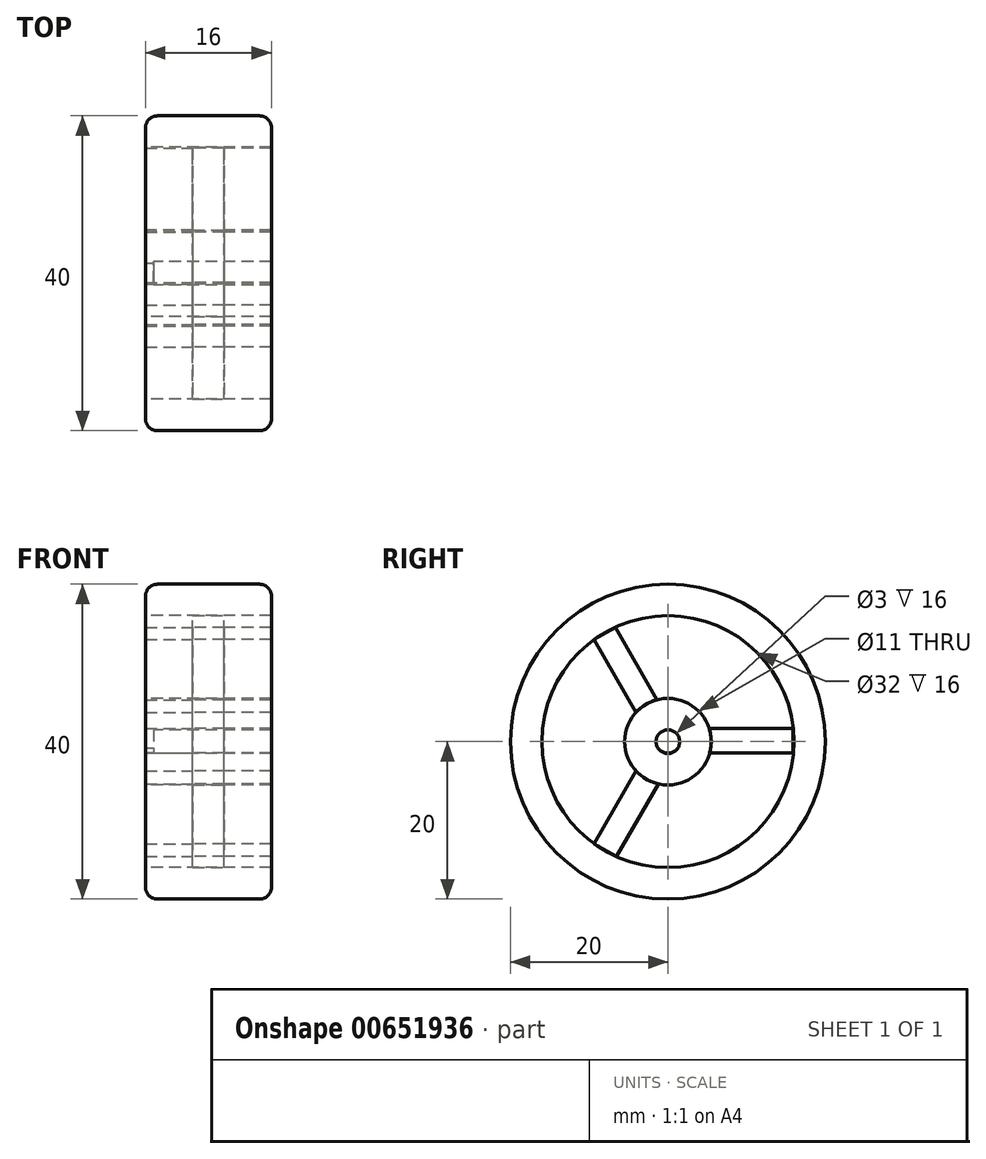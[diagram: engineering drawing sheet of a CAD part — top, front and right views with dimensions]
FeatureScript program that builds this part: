
annotation { "Feature Type Name" : "Feature", "Feature Type Description" : "" }
export const myFeature = defineFeature(function(context is Context, id is Id, definition is map)
    precondition{}
    {
        {
            var Q0;
            Q0=qCreatedBy(makeId("Front.planeOp"),FACE);
            var sketch = newSketch(context, id + "F0", { "sketchPlane" : qUnion([Q0])});
            skLineSegment(sketch, "E0.bottom", {"start": v(0, 0) * mm, "end": v(16, 0) * mm});
            skLineSegment(sketch, "E1.bottom", {"start": v(6, 0) * mm, "end": v(10, 0) * mm});
            skLineSegment(sketch, "E1.top", {"start": v(6, -16) * mm, "end": v(10, -16) * mm});
            skLineSegment(sketch, "E1.left", {"start": v(6, -13) * mm, "end": v(6, -14.5) * mm});
            skLineSegment(sketch, "E1.right", {"start": v(10, -13) * mm, "end": v(10, -14.5) * mm});
            skLineSegment(sketch, "E2.bottom", {"start": v(0, -16) * mm, "end": v(16, -16) * mm, "construction": true});
            skLineSegment(sketch, "E2.top", {"start": v(0, -13) * mm, "end": v(16, -13) * mm});
            skLineSegment(sketch, "E2.left", {"start": v(0, -14.5) * mm, "end": v(0, -13) * mm});
            skLineSegment(sketch, "E3", {"start": v(16, -14.5) * mm, "end": v(0, -14.5) * mm});
            skLineSegment(sketch, "E4", {"start": v(16, -14.5) * mm, "end": v(16, -13) * mm});
            skLineSegment(sketch, "E5.bottom", {"start": v(10, -13) * mm, "end": v(6, -13) * mm});
            skLineSegment(sketch, "E5.top", {"start": v(10, -10.5) * mm, "end": v(6, -10.5) * mm});
            skLineSegment(sketch, "E5.left", {"start": v(10, -13) * mm, "end": v(10, -10.5) * mm});
            skLineSegment(sketch, "E5.right", {"start": v(6, -13) * mm, "end": v(6, -10.5) * mm});
            skArc(sketch, "E6", {"start": v(1.5, 4) * mm, "mid": v(0.44, 3.56) * mm, "end": v(0, 2.5) * mm});
            skLineSegment(sketch, "E7", {"start": v(16, 4.74) * mm, "end": v(14.5, 4.74) * mm});
            skArc(sketch, "E8", {"start": v(16, 2.5) * mm, "mid": v(15.56, 3.56) * mm, "end": v(14.5, 4) * mm});
            skLineSegment(sketch, "E9", {"start": v(0, 2.5) * mm, "end": v(0, 0) * mm});
            skLineSegment(sketch, "E10", {"start": v(16, 0) * mm, "end": v(16, 2.5) * mm});
            skLineSegment(sketch, "E11", {"start": v(14.5, 4) * mm, "end": v(1.5, 4) * mm});
            skPoint(sketch, "E12.end.orphan", {"position": v(8, 0) * mm});
            skPoint(sketch, "E12.start.orphan", {"position": v(8, -10.5) * mm});
            skSolve(sketch);
        }
        {
            var Q0;
            Q0=qSketchRegion(id+"F0",true);
            var Q1;
            Q1=sQuery(id+"F0.wireOp",EDGE,"E1.top");
            revolve(context, id + "F1", {"entities" : qUnion([Q0]), "axis" : qUnion([Q1]), "revolveType" : RevolveType.FULL});
        }
        {
            var Q0;
            Q0=makeQuery(id+"F1.opRevolve","SWEPT_FACE",FACE,{"disambiguationData":[OSD([sQuery(id+"F0.wireOp",EDGE,"E5.right"),sQuery(id+"F0.wireOp",EDGE,"ZnnQBpbw-xC8R-MT8B-JQXv-VcrKk8POS6gG")])]});
            var sketch = newSketch(context, id + "F2", { "sketchPlane" : qUnion([Q0])});
            skLineSegment(sketch, "E13", {"start": v(-2.5, -14.35) * mm, "end": v(-15.91, -14.35) * mm});
            skLineSegment(sketch, "E14.1.1", {"start": v(-0.18, -19) * mm, "end": v(6.53, -30.6) * mm});
            skLineSegment(sketch, "E14.2.1", {"start": v(2.68, -14.65) * mm, "end": v(9.39, -3.04) * mm});
            skPoint(sketch, "E14.center", {"position": v(0, -16) * mm});
            skLineSegment(sketch, "E15", {"start": v(-15.91, -14.35) * mm, "end": v(-15.91, -17.46) * mm});
            skLineSegment(sketch, "E16", {"start": v(-15.91, -17.46) * mm, "end": v(-2.62, -17.46) * mm});
            skLineSegment(sketch, "E17", {"start": v(9.39, -3.04) * mm, "end": v(6.7, -1.49) * mm});
            skLineSegment(sketch, "E18", {"start": v(6.53, -30.6) * mm, "end": v(9.37, -28.97) * mm});
            skPoint(sketch, "E18.endSnap0", {"position": v(9.37, -29.3) * mm});
            skLineSegment(sketch, "E19", {"start": v(9.37, -28.97) * mm, "end": v(2.73, -17.46) * mm});
            skLineSegment(sketch, "E20", {"start": v(6.7, -1.49) * mm, "end": v(0.04, -13) * mm});
            skSolve(sketch);
        }
        {
            var Q0;
            {var subQ0=sQuery(id+"F2.wireOp",EDGE,"E17");Q0=makeQuery(id+"F2.imprint","IMPRINT",FACE,{"disambiguationData":[TD([[makeQuery(id+"F2.imprint","IMPRINT",EDGE,{"derivedFrom":subQ0}),1.0]])]});}
            var Q1;
            {var subQ0=sQuery(id+"F2.wireOp",EDGE,"E18");Q1=makeQuery(id+"F2.imprint","IMPRINT",FACE,{"disambiguationData":[TD([[makeQuery(id+"F2.imprint","IMPRINT",EDGE,{"derivedFrom":subQ0}),1.0]])]});}
            var Q2;
            {var subQ0=sQuery(id+"F2.wireOp",EDGE,"E15");Q2=makeQuery(id+"F2.imprint","IMPRINT",FACE,{"disambiguationData":[TD([[makeQuery(id+"F2.imprint","IMPRINT",EDGE,{"derivedFrom":subQ0}),1.0]])]});}
            extrude(context, id + "F3", {"entities" : qUnion([Q0, Q1, Q2]), "operationType" : NewBodyOperationType.ADD, "oppositeDirection" : true, "depth" : 4 * mm});
        }
        {
            var Q0;
            Q0=qCreatedBy(makeId("Right.planeOp"),FACE);
            var sketch = newSketch(context, id + "F4", { "sketchPlane" : qUnion([Q0])});
            skCircle(sketch, "E21", {"center": v(0, -15.89) * mm, "radius": 1.57 * mm});
            skSolve(sketch);
        }
        {
            var Q0;
            Q0=makeQuery(id+"F4.imprint","IMPRINT",FACE,{"disambiguationData":[TD([[makeQuery(id+"F4.imprint","IMPRINT",EDGE,{"derivedFrom":sQuery(id+"F4.wireOp",EDGE,"E21")}),1.0]])]});
            var Q1;
            Q1=sQuery(id+"F4.wireOp",EDGE,"E21");
            extrude(context, id + "F5", {"entities" : qUnion([Q0]), "operationType" : NewBodyOperationType.ADD, "surfaceEntities" : qUnion([Q1]), "depth" : 1 * mm});
        }
        {
            var Q0;
            {var subQ0=sQuery(id+"F0.wireOp",EDGE,"E5.right");var subQ1=sQuery(id+"F0.wireOp",EDGE,"E5.top");Q0=makeQuery(id+"F3.boolean.opBoolean","MERGE",FACE,{"derivedFrom":[makeQuery(id+"F1.opRevolve","SWEPT_FACE",FACE,{"disambiguationData":[OSD([subQ0])]}),makeQuery(id+"F3.opExtrude","CAP_FACE",FACE,{"disambiguationData":[OSD([subQ1,subQ0,sQuery(id+"F2.wireOp",EDGE,"E13"),sQuery(id+"F2.wireOp",EDGE,"E15"),sQuery(id+"F2.wireOp",EDGE,"E16")])],"isStart":true}),makeQuery(id+"F3.opExtrude","CAP_FACE",FACE,{"disambiguationData":[OSD([subQ1,subQ0,sQuery(id+"F2.wireOp",EDGE,"E14.1.1"),sQuery(id+"F2.wireOp",EDGE,"E18"),sQuery(id+"F2.wireOp",EDGE,"E19")])],"isStart":true}),makeQuery(id+"F3.opExtrude","CAP_FACE",FACE,{"disambiguationData":[OSD([subQ1,subQ0,sQuery(id+"F2.wireOp",EDGE,"E14.2.1"),sQuery(id+"F2.wireOp",EDGE,"E17"),sQuery(id+"F2.wireOp",EDGE,"E20")])],"isStart":true})]});}
            var sketch = newSketch(context, id + "F6", { "sketchPlane" : qUnion([Q0])});
            skCircle(sketch, "E22", {"center": v(0, -16) * mm, "radius": 5.5 * mm});
            skSolve(sketch);
        }
        {
            var Q0;
            Q0=makeQuery(id+"F6.imprint","IMPRINT",FACE,{"disambiguationData":[TD([[makeQuery(id+"F6.imprint","IMPRINT",EDGE,{"derivedFrom":makeQuery(id+"F1.opRevolve","SWEPT_EDGE",EDGE,{"disambiguationData":[OSD([sQuery(id+"F0.wireOp",EDGE,"E1.left"),sQuery(id+"F0.wireOp",EDGE,"E2.top"),sQuery(id+"F0.wireOp",EDGE,"E5.bottom"),sQuery(id+"F0.wireOp",EDGE,"E5.right")])]})}),-1.0]])]});
            extrude(context, id + "F7", {"entities" : qUnion([Q0]), "operationType" : NewBodyOperationType.ADD, "depth" : 6 * mm, "offsetDistance" : 25 * mm});
        }
        {
            var Q0;
            {var subQ0=sQuery(id+"F0.wireOp",EDGE,"E5.right");var subQ1=sQuery(id+"F0.wireOp",EDGE,"E5.top");Q0=makeQuery(id+"F3.boolean.opBoolean","MERGE",FACE,{"derivedFrom":[makeQuery(id+"F1.opRevolve","SWEPT_FACE",FACE,{"disambiguationData":[OSD([sQuery(id+"F0.wireOp",EDGE,"E5.left")])]}),makeQuery(id+"F3.opExtrude","CAP_FACE",FACE,{"disambiguationData":[OSD([subQ1,subQ0,sQuery(id+"F2.wireOp",EDGE,"E13"),sQuery(id+"F2.wireOp",EDGE,"E15"),sQuery(id+"F2.wireOp",EDGE,"E16")])],"isStart":false}),makeQuery(id+"F3.opExtrude","CAP_FACE",FACE,{"disambiguationData":[OSD([subQ1,subQ0,sQuery(id+"F2.wireOp",EDGE,"E14.1.1"),sQuery(id+"F2.wireOp",EDGE,"E18"),sQuery(id+"F2.wireOp",EDGE,"E19")])],"isStart":false}),makeQuery(id+"F3.opExtrude","CAP_FACE",FACE,{"disambiguationData":[OSD([subQ1,subQ0,sQuery(id+"F2.wireOp",EDGE,"E14.2.1"),sQuery(id+"F2.wireOp",EDGE,"E17"),sQuery(id+"F2.wireOp",EDGE,"E20")])],"isStart":false})]});}
            var sketch = newSketch(context, id + "F8", { "sketchPlane" : qUnion([Q0])});
            skCircle(sketch, "E23", {"center": v(0, -16) * mm, "radius": 5.5 * mm});
            skSolve(sketch);
        }
        {
            var Q0;
            Q0=makeQuery(id+"F8.imprint","IMPRINT",FACE,{"disambiguationData":[TD([[makeQuery(id+"F8.imprint","IMPRINT",EDGE,{"derivedFrom":makeQuery(id+"F1.opRevolve","SWEPT_EDGE",EDGE,{"disambiguationData":[OSD([sQuery(id+"F0.wireOp",EDGE,"E1.right"),sQuery(id+"F0.wireOp",EDGE,"E2.top"),sQuery(id+"F0.wireOp",EDGE,"E5.bottom"),sQuery(id+"F0.wireOp",EDGE,"E5.left")])]})}),1.0]])]});
            extrude(context, id + "F9", {"entities" : qUnion([Q0]), "operationType" : NewBodyOperationType.ADD, "depth" : 6 * mm, "offsetDistance" : 25 * mm});
        }
        {
            var Q0;
            Q0=makeQuery(id+"F3.opExtrude","SWEPT_FACE",FACE,{"disambiguationData":[OSD([sQuery(id+"F2.wireOp",EDGE,"E14.2.1")])]});
            var Q1;
            {var subQ2=sQuery(id+"F2.wireOp",EDGE,"E13");var subQ4=sQuery(id+"F0.wireOp",EDGE,"E5.top");var subQ10=sQuery(id+"F2.wireOp",EDGE,"E14.2.1");var subQ13=sQuery(id+"F2.wireOp",EDGE,"E14.1.1");var subQ19=makeQuery(id+"F1.opRevolve","SWEPT_FACE",FACE,{"disambiguationData":[OSD([subQ4])]});Q1=makeQuery(id+"F9.boolean.opBoolean","MERGE",FACE,{"derivedFrom":[makeQuery(id+"F7.boolean.opBoolean","MERGE",FACE,{"derivedFrom":[makeQuery(id+"F3.boolean.opBoolean","SPLIT",FACE,{"disambiguationData":[TD([makeQuery(id+"F3.opExtrude","SWEPT_FACE",FACE,{"disambiguationData":[OSD([subQ10])]})])],"derivedFrom":subQ19}),makeQuery(id+"F3.boolean.opBoolean","SPLIT",FACE,{"disambiguationData":[TD([makeQuery(id+"F3.opExtrude","SWEPT_FACE",FACE,{"disambiguationData":[OSD([subQ2])]})])],"derivedFrom":subQ19}),makeQuery(id+"F3.boolean.opBoolean","SPLIT",FACE,{"disambiguationData":[TD([makeQuery(id+"F3.opExtrude","SWEPT_FACE",FACE,{"disambiguationData":[OSD([subQ13])]})])],"derivedFrom":subQ19}),makeQuery(id+"F7.opExtrude","SWEPT_FACE",FACE,{"disambiguationData":[OSD([sQuery(id+"F6.wireOp",EDGE,"E22")])]})]}),makeQuery(id+"F9.opExtrude","SWEPT_FACE",FACE,{"disambiguationData":[OSD([sQuery(id+"F8.wireOp",EDGE,"E23")])]})]});}
            revolve(context, id + "F10", {"surfaceOperationType" : NewSurfaceOperationType.NEW, "entities" : qUnion([Q0]), "axis" : qUnion([Q1]), "revolveType" : RevolveType.FULL});
        }
        {
            var Q0;
            {var subQ0=sQuery(id+"F2.wireOp",EDGE,"E15");var subQ1=sQuery(id+"F2.wireOp",EDGE,"E16");var subQ2=sQuery(id+"F2.wireOp",EDGE,"E13");var subQ3=sQuery(id+"F0.wireOp",EDGE,"E5.top");var subQ4=sQuery(id+"F0.wireOp",EDGE,"E5.right");Q0=makeQuery(id+"F7.boolean.opBoolean","SPLIT",FACE,{"disambiguationData":[TD([makeQuery(id+"F3.opExtrude","SWEPT_FACE",FACE,{"disambiguationData":[OSD([subQ2])]})])],"derivedFrom":makeQuery(id+"F3.boolean.opBoolean","MERGE",FACE,{"derivedFrom":[makeQuery(id+"F1.opRevolve","SWEPT_FACE",FACE,{"disambiguationData":[OSD([subQ4])]}),makeQuery(id+"F3.opExtrude","CAP_FACE",FACE,{"disambiguationData":[OSD([subQ3,subQ4,subQ2,subQ0,subQ1])],"isStart":true}),makeQuery(id+"F3.opExtrude","CAP_FACE",FACE,{"disambiguationData":[OSD([subQ3,subQ4,sQuery(id+"F2.wireOp",EDGE,"E14.1.1"),sQuery(id+"F2.wireOp",EDGE,"E18"),sQuery(id+"F2.wireOp",EDGE,"E19")])],"isStart":true}),makeQuery(id+"F3.opExtrude","CAP_FACE",FACE,{"disambiguationData":[OSD([subQ3,subQ4,sQuery(id+"F2.wireOp",EDGE,"E14.2.1"),sQuery(id+"F2.wireOp",EDGE,"E17"),sQuery(id+"F2.wireOp",EDGE,"E20")])],"isStart":true})]})});}
            var Q1;
            {var subQ0=sQuery(id+"F2.wireOp",EDGE,"E20");var subQ1=sQuery(id+"F2.wireOp",EDGE,"E14.2.1");var subQ2=sQuery(id+"F2.wireOp",EDGE,"E17");var subQ3=sQuery(id+"F0.wireOp",EDGE,"E5.top");var subQ4=sQuery(id+"F0.wireOp",EDGE,"E5.right");Q1=makeQuery(id+"F7.boolean.opBoolean","SPLIT",FACE,{"disambiguationData":[TD([makeQuery(id+"F3.opExtrude","SWEPT_FACE",FACE,{"disambiguationData":[OSD([subQ1])]})])],"derivedFrom":makeQuery(id+"F3.boolean.opBoolean","MERGE",FACE,{"derivedFrom":[makeQuery(id+"F1.opRevolve","SWEPT_FACE",FACE,{"disambiguationData":[OSD([subQ4])]}),makeQuery(id+"F3.opExtrude","CAP_FACE",FACE,{"disambiguationData":[OSD([subQ3,subQ4,sQuery(id+"F2.wireOp",EDGE,"E13"),sQuery(id+"F2.wireOp",EDGE,"E15"),sQuery(id+"F2.wireOp",EDGE,"E16")])],"isStart":true}),makeQuery(id+"F3.opExtrude","CAP_FACE",FACE,{"disambiguationData":[OSD([subQ3,subQ4,sQuery(id+"F2.wireOp",EDGE,"E14.1.1"),sQuery(id+"F2.wireOp",EDGE,"E18"),sQuery(id+"F2.wireOp",EDGE,"E19")])],"isStart":true}),makeQuery(id+"F3.opExtrude","CAP_FACE",FACE,{"disambiguationData":[OSD([subQ3,subQ4,subQ1,subQ2,subQ0])],"isStart":true})]})});}
            var Q2;
            {var subQ0=sQuery(id+"F2.wireOp",EDGE,"E19");var subQ1=sQuery(id+"F2.wireOp",EDGE,"E18");var subQ2=sQuery(id+"F2.wireOp",EDGE,"E14.1.1");var subQ3=sQuery(id+"F0.wireOp",EDGE,"E5.top");var subQ4=sQuery(id+"F0.wireOp",EDGE,"E5.right");Q2=makeQuery(id+"F7.boolean.opBoolean","SPLIT",FACE,{"disambiguationData":[TD([makeQuery(id+"F3.opExtrude","SWEPT_FACE",FACE,{"disambiguationData":[OSD([subQ2])]})])],"derivedFrom":makeQuery(id+"F3.boolean.opBoolean","MERGE",FACE,{"derivedFrom":[makeQuery(id+"F1.opRevolve","SWEPT_FACE",FACE,{"disambiguationData":[OSD([subQ4])]}),makeQuery(id+"F3.opExtrude","CAP_FACE",FACE,{"disambiguationData":[OSD([subQ3,subQ4,sQuery(id+"F2.wireOp",EDGE,"E13"),sQuery(id+"F2.wireOp",EDGE,"E15"),sQuery(id+"F2.wireOp",EDGE,"E16")])],"isStart":true}),makeQuery(id+"F3.opExtrude","CAP_FACE",FACE,{"disambiguationData":[OSD([subQ3,subQ4,subQ2,subQ1,subQ0])],"isStart":true}),makeQuery(id+"F3.opExtrude","CAP_FACE",FACE,{"disambiguationData":[OSD([subQ3,subQ4,sQuery(id+"F2.wireOp",EDGE,"E14.2.1"),sQuery(id+"F2.wireOp",EDGE,"E17"),sQuery(id+"F2.wireOp",EDGE,"E20")])],"isStart":true})]})});}
            extrude(context, id + "F11", {"entities" : qUnion([Q0, Q1, Q2]), "depth" : 6 * mm, "offsetDistance" : 25 * mm});
        }
        {
            var Q0;
            {var subQ0=sQuery(id+"F2.wireOp",EDGE,"E20");var subQ1=sQuery(id+"F2.wireOp",EDGE,"E14.2.1");var subQ2=sQuery(id+"F2.wireOp",EDGE,"E17");var subQ3=sQuery(id+"F0.wireOp",EDGE,"E5.top");var subQ4=sQuery(id+"F0.wireOp",EDGE,"E5.right");Q0=makeQuery(id+"F9.boolean.opBoolean","SPLIT",FACE,{"disambiguationData":[TD([makeQuery(id+"F3.opExtrude","SWEPT_FACE",FACE,{"disambiguationData":[OSD([subQ1])]})])],"derivedFrom":makeQuery(id+"F3.boolean.opBoolean","MERGE",FACE,{"derivedFrom":[makeQuery(id+"F1.opRevolve","SWEPT_FACE",FACE,{"disambiguationData":[OSD([sQuery(id+"F0.wireOp",EDGE,"E5.left")])]}),makeQuery(id+"F3.opExtrude","CAP_FACE",FACE,{"disambiguationData":[OSD([subQ3,subQ4,sQuery(id+"F2.wireOp",EDGE,"E13"),sQuery(id+"F2.wireOp",EDGE,"E15"),sQuery(id+"F2.wireOp",EDGE,"E16")])],"isStart":false}),makeQuery(id+"F3.opExtrude","CAP_FACE",FACE,{"disambiguationData":[OSD([subQ3,subQ4,sQuery(id+"F2.wireOp",EDGE,"E14.1.1"),sQuery(id+"F2.wireOp",EDGE,"E18"),sQuery(id+"F2.wireOp",EDGE,"E19")])],"isStart":false}),makeQuery(id+"F3.opExtrude","CAP_FACE",FACE,{"disambiguationData":[OSD([subQ3,subQ4,subQ1,subQ2,subQ0])],"isStart":false})]})});}
            var Q1;
            {var subQ0=sQuery(id+"F2.wireOp",EDGE,"E19");var subQ1=sQuery(id+"F2.wireOp",EDGE,"E18");var subQ2=sQuery(id+"F2.wireOp",EDGE,"E14.1.1");var subQ3=sQuery(id+"F0.wireOp",EDGE,"E5.top");var subQ4=sQuery(id+"F0.wireOp",EDGE,"E5.right");Q1=makeQuery(id+"F9.boolean.opBoolean","SPLIT",FACE,{"disambiguationData":[TD([makeQuery(id+"F3.opExtrude","SWEPT_FACE",FACE,{"disambiguationData":[OSD([subQ2])]})])],"derivedFrom":makeQuery(id+"F3.boolean.opBoolean","MERGE",FACE,{"derivedFrom":[makeQuery(id+"F1.opRevolve","SWEPT_FACE",FACE,{"disambiguationData":[OSD([sQuery(id+"F0.wireOp",EDGE,"E5.left")])]}),makeQuery(id+"F3.opExtrude","CAP_FACE",FACE,{"disambiguationData":[OSD([subQ3,subQ4,sQuery(id+"F2.wireOp",EDGE,"E13"),sQuery(id+"F2.wireOp",EDGE,"E15"),sQuery(id+"F2.wireOp",EDGE,"E16")])],"isStart":false}),makeQuery(id+"F3.opExtrude","CAP_FACE",FACE,{"disambiguationData":[OSD([subQ3,subQ4,subQ2,subQ1,subQ0])],"isStart":false}),makeQuery(id+"F3.opExtrude","CAP_FACE",FACE,{"disambiguationData":[OSD([subQ3,subQ4,sQuery(id+"F2.wireOp",EDGE,"E14.2.1"),sQuery(id+"F2.wireOp",EDGE,"E17"),sQuery(id+"F2.wireOp",EDGE,"E20")])],"isStart":false})]})});}
            var Q2;
            {var subQ0=sQuery(id+"F2.wireOp",EDGE,"E15");var subQ1=sQuery(id+"F2.wireOp",EDGE,"E16");var subQ2=sQuery(id+"F2.wireOp",EDGE,"E13");var subQ3=sQuery(id+"F0.wireOp",EDGE,"E5.top");var subQ4=sQuery(id+"F0.wireOp",EDGE,"E5.right");Q2=makeQuery(id+"F9.boolean.opBoolean","SPLIT",FACE,{"disambiguationData":[TD([makeQuery(id+"F3.opExtrude","SWEPT_FACE",FACE,{"disambiguationData":[OSD([subQ2])]})])],"derivedFrom":makeQuery(id+"F3.boolean.opBoolean","MERGE",FACE,{"derivedFrom":[makeQuery(id+"F1.opRevolve","SWEPT_FACE",FACE,{"disambiguationData":[OSD([sQuery(id+"F0.wireOp",EDGE,"E5.left")])]}),makeQuery(id+"F3.opExtrude","CAP_FACE",FACE,{"disambiguationData":[OSD([subQ3,subQ4,subQ2,subQ0,subQ1])],"isStart":false}),makeQuery(id+"F3.opExtrude","CAP_FACE",FACE,{"disambiguationData":[OSD([subQ3,subQ4,sQuery(id+"F2.wireOp",EDGE,"E14.1.1"),sQuery(id+"F2.wireOp",EDGE,"E18"),sQuery(id+"F2.wireOp",EDGE,"E19")])],"isStart":false}),makeQuery(id+"F3.opExtrude","CAP_FACE",FACE,{"disambiguationData":[OSD([subQ3,subQ4,sQuery(id+"F2.wireOp",EDGE,"E14.2.1"),sQuery(id+"F2.wireOp",EDGE,"E17"),sQuery(id+"F2.wireOp",EDGE,"E20")])],"isStart":false})]})});}
            extrude(context, id + "F12", {"entities" : qUnion([Q0, Q1, Q2]), "depth" : 6 * mm, "offsetDistance" : 25 * mm});
        }
    });
